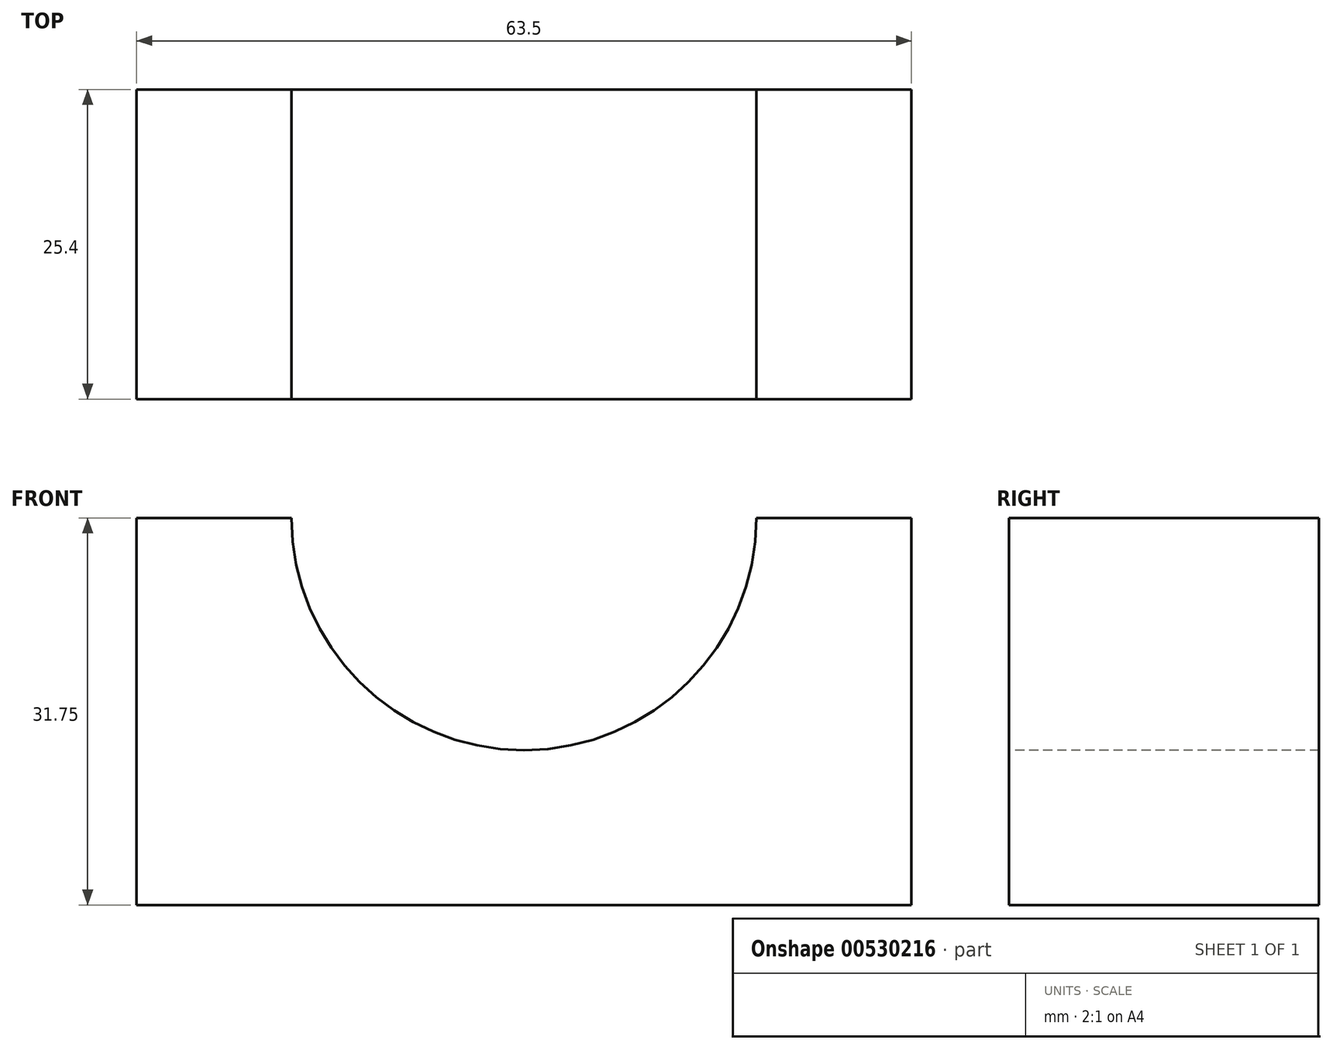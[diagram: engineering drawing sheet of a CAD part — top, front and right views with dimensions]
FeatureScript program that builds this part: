
annotation { "Feature Type Name" : "Feature", "Feature Type Description" : "" }
export const myFeature = defineFeature(function(context is Context, id is Id, definition is map)
    precondition{}
    {
        {
            var Q0;
            Q0=qCreatedBy(makeId("Front.planeOp"),FACE);
            var sketch = newSketch(context, id + "F0", { "sketchPlane" : qUnion([Q0])});
            skLineSegment(sketch, "E0", {"start": v(0, 0) * mm, "end": v(-63.5, 0) * mm});
            skLineSegment(sketch, "E1", {"start": v(-63.5, 0) * mm, "end": v(-63.5, 31.75) * mm});
            skLineSegment(sketch, "E2", {"start": v(-63.5, 31.75) * mm, "end": v(0, 31.75) * mm});
            skLineSegment(sketch, "E3", {"start": v(0, 31.75) * mm, "end": v(0, 0) * mm});
            skSolve(sketch);
        }
        {
            var Q0;
            Q0=makeQuery(id+"F0.imprint","IMPRINT",FACE,{"disambiguationData":[TD([[makeQuery(id+"F0.imprint","IMPRINT",EDGE,{"derivedFrom":sQuery(id+"F0.wireOp",EDGE,"E0")}),-1.0]])]});
            extrude(context, id + "F1", {"entities" : qUnion([Q0]), "depth" : 25.4 * mm, "offsetDistance" : 25.4 * mm});
        }
        {
            var Q0;
            Q0=makeQuery(id+"F1.opExtrude","CAP_FACE",FACE,{"disambiguationData":[OSD([sQuery(id+"F0.wireOp",EDGE,"E0"),sQuery(id+"F0.wireOp",EDGE,"E1"),sQuery(id+"F0.wireOp",EDGE,"E2"),sQuery(id+"F0.wireOp",EDGE,"E3")])],"isStart":false});
            var sketch = newSketch(context, id + "F2", { "sketchPlane" : qUnion([Q0])});
            skCircle(sketch, "E4", {"center": v(-31.75, 31.75) * mm, "radius": 19.05 * mm});
            skSolve(sketch);
        }
        {
            var Q0;
            {var subQ0=sQuery(id+"F2.wireOp",EDGE,"E4");var subQ1=makeQuery(id+"F1.opExtrude","CAP_EDGE",EDGE,{"disambiguationData":[OSD([sQuery(id+"F0.wireOp",EDGE,"E2")])],"isStart":false});var subQ2=makeQuery(id+"F2.imprint","INTERSECT",VERTEX,{"disambiguationData":[OD(0.0)],"derivedFrom":[subQ1,subQ0]});Q0=makeQuery(id+"F2.imprint","IMPRINT",FACE,{"disambiguationData":[TD([[makeQuery(id+"F2.imprint","IMPRINT",EDGE,{"disambiguationData":[TD([[subQ2,-1.0]])],"derivedFrom":subQ0}),1.0]])]});}
            extrude(context, id + "F3", {"entities" : qUnion([Q0]), "operationType" : NewBodyOperationType.REMOVE, "oppositeDirection" : true, "depth" : 25.4 * mm, "offsetDistance" : 25.4 * mm});
        }
    });
